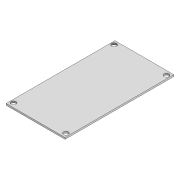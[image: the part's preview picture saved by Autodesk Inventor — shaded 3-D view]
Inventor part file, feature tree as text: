
AUTODESK INVENTOR PART (.ipt)
format: ipt  version: 2022 (Build 260153000, 153)  size: 95,744 bytes
history: native  units: mm
features: sketch x2, extrude x1, hole x1, projected_geometry x1
ambient origin geometry x8: Origin, YZ Plane, XZ Plane, XY Plane, X Axis, Y Axis, Z Axis, Center Point
bodies: Solid1 (feature_tree)
feature tree (5):
  extrude  "Extrusion1"  Depth=66.5mm
  hole  "Hole1"  [1 undecoded]
  sketch  "Sketch1"  dims[d0=36.0mm d1=66.5mm]
  sketch  "Sketch2"  dims[d2=1.0mm d3=0.0mm d11=3.0mm d12=3.0mm d13=3.0mm d14=3.0mm d17=0.5mm d18=1.0mm d19=3.0mm d20=6.0mm d21=4.0mm d22=2.0mm d23=90.0deg d24=6.0mm d25=0.0mm]
  projected_geometry  "Project Cut Edges1"
note: 1 required parameter value undecoded (feature->parameter linkage not recoverable at this tier; creation-order binding heuristic only, values carry confidence <= 0.55)
